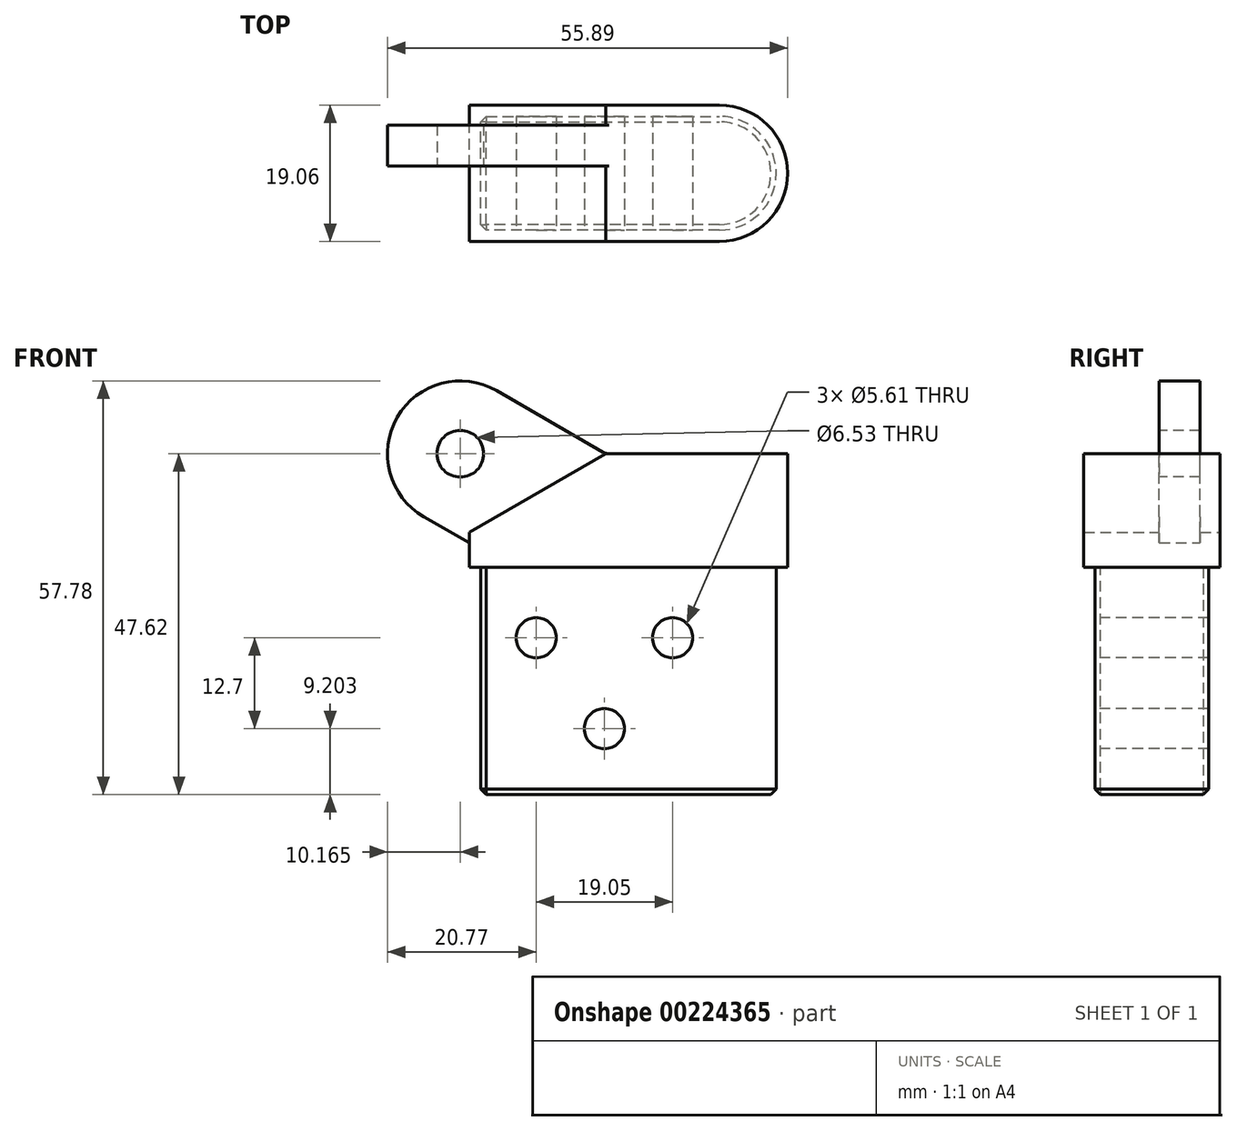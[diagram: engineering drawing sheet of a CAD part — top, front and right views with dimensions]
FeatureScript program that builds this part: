
annotation { "Feature Type Name" : "Feature", "Feature Type Description" : "" }
export const myFeature = defineFeature(function(context is Context, id is Id, definition is map)
    precondition{}
    {
        {
            var Q0;
            Q0=qCreatedBy(makeId("Top.planeOp"),FACE);
            var sketch = newSketch(context, id + "F0", { "sketchPlane" : qUnion([Q0])});
            skLineSegment(sketch, "E0", {"start": v(-34.92, 9.53) * mm, "end": v(0, 9.53) * mm});
            skArc(sketch, "E1", {"start": v(0, -9.53) * mm, "mid": v(9.53, 0) * mm, "end": v(0, 9.53) * mm});
            skLineSegment(sketch, "E2", {"start": v(0, -9.53) * mm, "end": v(-34.92, -9.53) * mm});
            skLineSegment(sketch, "E3", {"start": v(-34.92, -9.53) * mm, "end": v(-34.92, 9.53) * mm});
            skSolve(sketch);
        }
        {
            var Q0;
            Q0 = qSketchRegion(id + "F0", true);
            extrude(context, id + "F1", {"entities" : qUnion([Q0]), "oppositeDirection" : true, "depth" : 15.88 * mm});
        }
        {
            var Q0;
            Q0=makeQuery(id+"F1.opExtrude","CAP_FACE",FACE,{"disambiguationData":[OSD([sQuery(id+"F0.wireOp",EDGE,"E0"),sQuery(id+"F0.wireOp",EDGE,"E1"),sQuery(id+"F0.wireOp",EDGE,"E2"),sQuery(id+"F0.wireOp",EDGE,"E3")])],"isStart":false});
            var sketch = newSketch(context, id + "F2", { "sketchPlane" : qUnion([Q0])});
            skLineSegment(sketch, "E4.0", {"start": v(-33.34, 7.94) * mm, "end": v(-33.34, -7.94) * mm});
            skLineSegment(sketch, "E4.1", {"start": v(0, 7.94) * mm, "end": v(-33.34, 7.94) * mm});
            skArc(sketch, "E4.2", {"start": v(0, -7.94) * mm, "mid": v(7.94, 0) * mm, "end": v(0, 7.94) * mm});
            skLineSegment(sketch, "E4.3", {"start": v(-33.34, -7.94) * mm, "end": v(0, -7.94) * mm});
            skSolve(sketch);
        }
        {
            var Q0;
            Q0 = qSketchRegion(id + "F2", true);
            extrude(context, id + "F3", {"entities" : qUnion([Q0]), "operationType" : NewBodyOperationType.ADD, "depth" : 31.75 * mm});
        }
        {
            var Q0;
            Q0=makeQuery(id+"F1.opExtrude","CAP_EDGE",EDGE,{"disambiguationData":[OSD([sQuery(id+"F0.wireOp",EDGE,"E3")])],"isStart":true});
            chamfer(context, id + "F4", {"entities" : qUnion([Q0]), "chamferType" : ChamferType.OFFSET_ANGLE, "width" : 19.05 * mm, "oppositeDirection" : true, "angle" : 30 * degree, "tangentPropagation" : true});
        }
        {
            var Q0;
            Q0=makeQuery(id+"F1.opExtrude","SWEPT_FACE",FACE,{"disambiguationData":[OSD([sQuery(id+"F0.wireOp",EDGE,"E0")])]});
            var sketch = newSketch(context, id + "F5", { "sketchPlane" : qUnion([Q0])});
            skArc(sketch, "E5", {"start": v(41.28, -8.8) * mm, "mid": v(45, 5.08) * mm, "end": v(31.12, 8.8) * mm});
            skLineSegment(sketch, "E6", {"start": v(31.12, 8.8) * mm, "end": v(15.87, 0) * mm});
            skLineSegment(sketch, "E7", {"start": v(41.28, -8.8) * mm, "end": v(34.92, -12.46) * mm});
            skSolve(sketch);
        }
        {
            var Q0;
            Q0=makeQuery(id+"F5.imprint","IMPRINT",FACE,{"disambiguationData":[TD([[makeQuery(id+"F5.imprint","IMPRINT",EDGE,{"derivedFrom":sQuery(id+"F5.wireOp",EDGE,"E5")}),1.0]])]});
            extrude(context, id + "F6", {"entities" : qUnion([Q0]), "operationType" : NewBodyOperationType.ADD, "oppositeDirection" : true, "depth" : 8.5 * mm, "hasSecondDirection" : true, "secondDirectionOppositeDirection" : true, "secondDirectionDepth" : 2.8 * mm});
        }
        {
            var Q0;
            Q0=makeQuery(id+"F6.opExtrude","CAP_FACE",FACE,{"disambiguationData":[OSD([sQuery(id+"F0.wireOp",EDGE,"E0"),sQuery(id+"F0.wireOp",EDGE,"E3"),sQuery(id+"F5.wireOp",EDGE,"E5"),sQuery(id+"F5.wireOp",EDGE,"E6"),sQuery(id+"F5.wireOp",EDGE,"E7")])],"isStart":true});
            var sketch = newSketch(context, id + "F7", { "sketchPlane" : qUnion([Q0])});
            skPoint(sketch, "E8", {"position": v(36.2, 0) * mm});
            skSolve(sketch);
        }
        {
            var Q0;
            Q0=sQuery(id+"F7.wireOp",VERTEX,"E8");
            var Q1;
            Q1=makeQuery(id+"F1.opExtrude","SWEPT_BODY",BODY,{"disambiguationData":[OSD([sQuery(id+"F0.wireOp",EDGE,"E0"),sQuery(id+"F0.wireOp",EDGE,"E1"),sQuery(id+"F0.wireOp",EDGE,"E2"),sQuery(id+"F0.wireOp",EDGE,"E3")])]});
            hole(context, id + "F8", {"style" : HoleStyle.SIMPLE, "endStyle" : HoleEndStyle.THROUGH, "standardTappedOrClearance" : lookupTablePath({ "standard" : "ANSI", "fit" : "Close", "size" : "1/4", "type" : "Clearance" }), "standardBlindInLast" : lookupTablePath({ "fit" : "Close", "standard" : "ANSI", "size" : "1/4", "type" : "Clearance" }), "holeDiameter" : 6.53 * mm, "locations" : qUnion([Q0]), "scope" : qUnion([Q1]), "isTappedThrough" : true});
        }
        {
            var Q0;
            Q0=makeQuery(id+"F3.opExtrude","CAP_EDGE",EDGE,{"disambiguationData":[OSD([sQuery(id+"F2.wireOp",EDGE,"E4.1")])],"isStart":false});
            var Q1;
            Q1=makeQuery(id+"F3.opExtrude","CAP_EDGE",EDGE,{"disambiguationData":[OSD([sQuery(id+"F2.wireOp",EDGE,"E4.0")])],"isStart":false});
            var Q2;
            Q2=makeQuery(id+"F3.opExtrude","SWEPT_EDGE",EDGE,{"disambiguationData":[OSD([sQuery(id+"F2.wireOp",EDGE,"E4.0"),sQuery(id+"F2.wireOp",EDGE,"E4.1")])]});
            var Q3;
            Q3=makeQuery(id+"F3.opExtrude","SWEPT_EDGE",EDGE,{"disambiguationData":[OSD([sQuery(id+"F2.wireOp",EDGE,"E4.0"),sQuery(id+"F2.wireOp",EDGE,"E4.3")])]});
            chamfer(context, id + "F9", {"entities" : qUnion([Q0, Q1, Q2, Q3]), "width" : 0.76 * mm, "tangentPropagation" : true});
        }
        {
            var Q0;
            Q0=makeQuery(id+"F3.opExtrude","SWEPT_FACE",FACE,{"disambiguationData":[OSD([sQuery(id+"F2.wireOp",EDGE,"E4.3")])]});
            var sketch = newSketch(context, id + "F10", { "sketchPlane" : qUnion([Q0])});
            skPoint(sketch, "E9", {"position": v(25.6, -25.72) * mm});
            skPoint(sketch, "E10", {"position": v(6.54, -25.72) * mm});
            skPoint(sketch, "E11", {"position": v(16.07, -38.42) * mm});
            skLineSegment(sketch, "E12", {"start": v(6.54, -25.72) * mm, "end": v(25.6, -25.72) * mm, "construction": true});
            skLineSegment(sketch, "E13", {"start": v(16.07, -38.42) * mm, "end": v(16.07, -25.72) * mm, "construction": true});
            skSolve(sketch);
        }
        {
            var Q0;
            Q0=sQuery(id+"F10.wireOp",VERTEX,"E9");
            var Q1;
            Q1=sQuery(id+"F10.wireOp",VERTEX,"E10");
            var Q2;
            Q2=sQuery(id+"F10.wireOp",VERTEX,"E11");
            var Q3;
            Q3=makeQuery(id+"F1.opExtrude","SWEPT_BODY",BODY,{"disambiguationData":[OSD([sQuery(id+"F0.wireOp",EDGE,"E0"),sQuery(id+"F0.wireOp",EDGE,"E1"),sQuery(id+"F0.wireOp",EDGE,"E2"),sQuery(id+"F0.wireOp",EDGE,"E3")])]});
            hole(context, id + "F11", {"style" : HoleStyle.SIMPLE, "endStyle" : HoleEndStyle.THROUGH, "holeDiameter" : 5.61 * mm, "locations" : qUnion([Q0, Q1, Q2]), "scope" : qUnion([Q3]), "isTappedThrough" : true});
        }
        {
            var Q0;
            {var subQ0=sQuery(id+"F0.wireOp",EDGE,"E3");var subQ1=sQuery(id+"F0.wireOp",EDGE,"E0");Q0=makeQuery(id+"F6.boolean.opBoolean","MERGE",EDGE,{"derivedFrom":[makeQuery(id+"F4.opChamfer","BLEND_EDGE",EDGE,{"blendedFrom":[makeQuery(id+"F1.opExtrude","CAP_EDGE",EDGE,{"disambiguationData":[OSD([subQ0])],"isStart":true}),makeQuery(id+"F1.opExtrude","CAP_FACE",FACE,{"disambiguationData":[OSD([subQ1,sQuery(id+"F0.wireOp",EDGE,"E1"),sQuery(id+"F0.wireOp",EDGE,"E2"),subQ0])],"isStart":true})],"blendedInto":[makeQuery(id+"F1.opExtrude","CAP_FACE",FACE,{"disambiguationData":[OSD([subQ1,sQuery(id+"F0.wireOp",EDGE,"E1"),sQuery(id+"F0.wireOp",EDGE,"E2"),subQ0])],"isStart":true})]}),makeQuery(id+"F6.opExtrude","SWEPT_EDGE",EDGE,{"disambiguationData":[OSD([subQ1,subQ0,sQuery(id+"F5.wireOp",EDGE,"E6")])]})]});}
            var Q1;
            Q1=makeQuery(id+"F6.opExtrude","SWEPT_EDGE",EDGE,{"disambiguationData":[OSD([sQuery(id+"F0.wireOp",EDGE,"E0"),sQuery(id+"F0.wireOp",EDGE,"E3"),sQuery(id+"F5.wireOp",EDGE,"E7")])]});
            fillet(context, id + "F12", {"entities" : qUnion([Q0, Q1]), "radius" : 1.59 * mm, "tangentPropagation" : true, "allowEdgeOverflow" : false});
        }
    });
